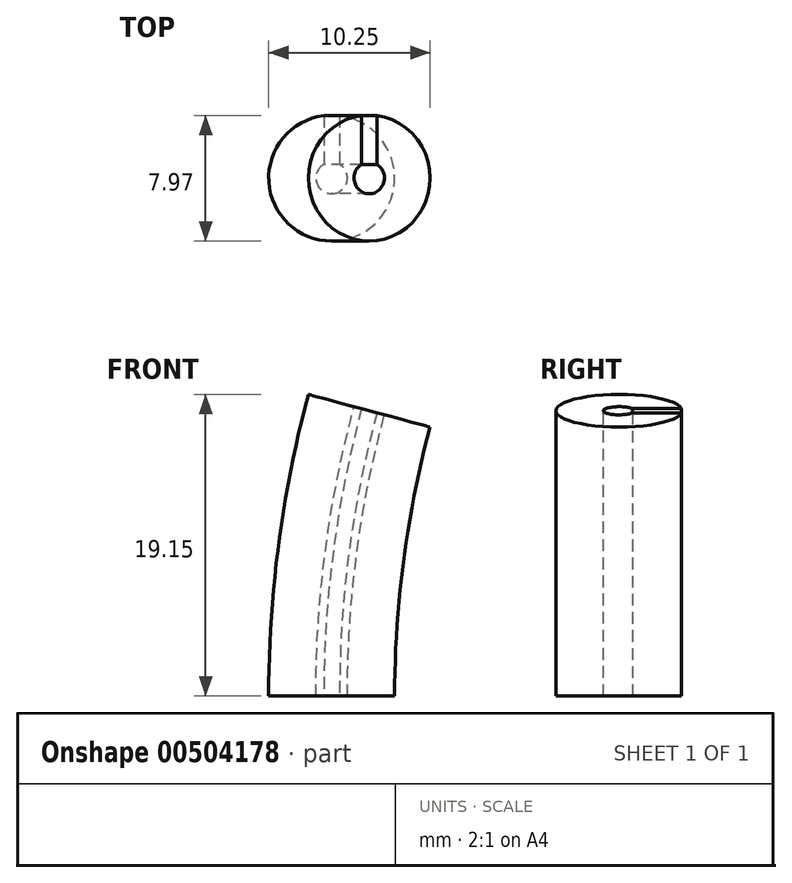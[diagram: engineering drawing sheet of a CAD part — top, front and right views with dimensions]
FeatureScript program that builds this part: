
annotation { "Feature Type Name" : "Feature", "Feature Type Description" : "" }
export const myFeature = defineFeature(function(context is Context, id is Id, definition is map)
    precondition{}
    {
        {
            var Q0;
            Q0=qCreatedBy(makeId("Top.planeOp"),FACE);
            var sketch = newSketch(context, id + "F0", { "sketchPlane" : qUnion([Q0])});
            skArc(sketch, "E0", {"start": v(-0.5, 0.87) * mm, "mid": v(0, -1) * mm, "end": v(0.5, 0.87) * mm});
            skArc(sketch, "E1", {"start": v(0.5, 3.97) * mm, "mid": v(0, -4) * mm, "end": v(-0.5, 3.97) * mm});
            skLineSegment(sketch, "E2", {"start": v(-0.5, 3.97) * mm, "end": v(-0.5, 0.87) * mm});
            skLineSegment(sketch, "E3", {"start": v(0.5, 3.97) * mm, "end": v(0.5, 0.87) * mm});
            skSolve(sketch);
        }
        {
            var Q0;
            Q0=qCreatedBy(makeId("Top.planeOp"),FACE);
            var sketch = newSketch(context, id + "F1", { "sketchPlane" : qUnion([Q0])});
            skLineSegment(sketch, "E4", {"start": v(70, 32.7) * mm, "end": v(70, -31.54) * mm});
            skSolve(sketch);
        }
        {
            var Q0;
            Q0 = qSketchRegion(id + "F0", true);
            var Q1;
            Q1=sQuery(id+"F1.wireOp",EDGE,"E4");
            revolve(context, id + "F2", {"entities" : qUnion([Q0]), "axis" : qUnion([Q1]), "revolveType" : RevolveType.ONE_DIRECTION, "oppositeDirection" : true, "angle" : 15 * degree});
        }
    });
